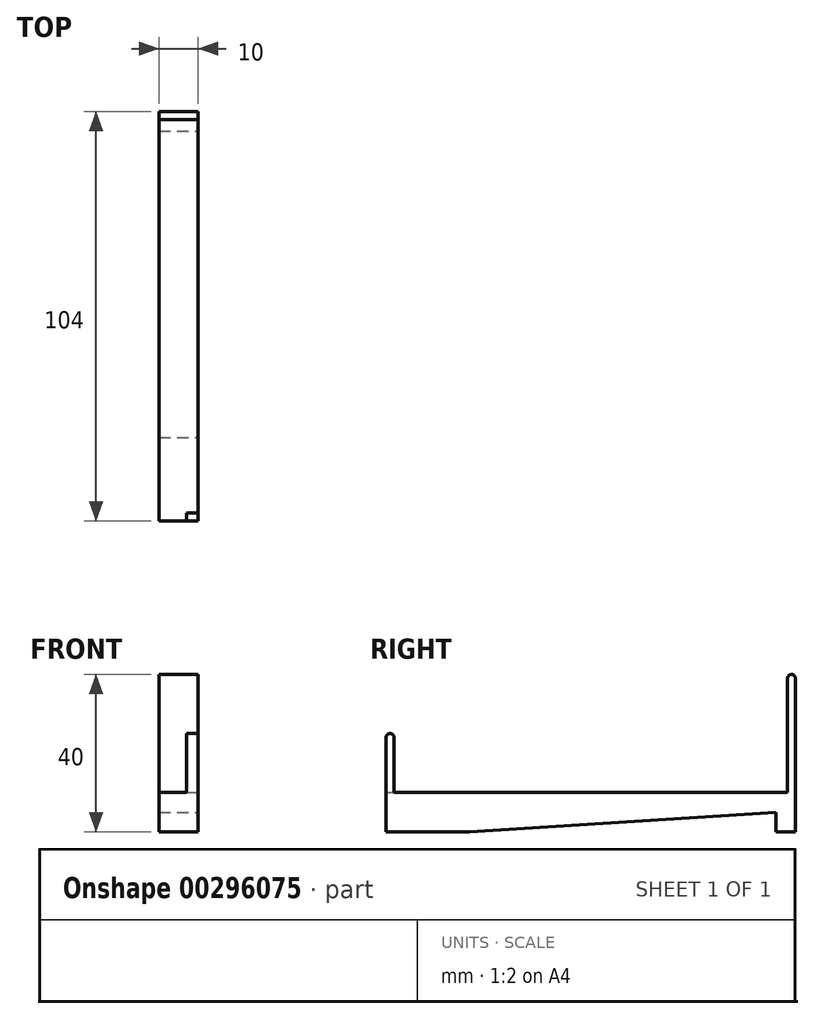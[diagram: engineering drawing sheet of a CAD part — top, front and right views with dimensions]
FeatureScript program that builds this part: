
annotation { "Feature Type Name" : "Feature", "Feature Type Description" : "" }
export const myFeature = defineFeature(function(context is Context, id is Id, definition is map)
    precondition{}
    {
        {
            var Q0;
            Q0=qCreatedBy(makeId("Top.planeOp"),FACE);
            var sketch = newSketch(context, id + "F0", { "sketchPlane" : qUnion([Q0])});
            skLineSegment(sketch, "E0.bottom", {"start": v(5, -52) * mm, "end": v(-5, -52) * mm});
            skLineSegment(sketch, "E0.top", {"start": v(5, 52) * mm, "end": v(-5, 52) * mm});
            skLineSegment(sketch, "E0.left", {"start": v(5, -52) * mm, "end": v(5, 52) * mm});
            skLineSegment(sketch, "E0.right", {"start": v(-5, -52) * mm, "end": v(-5, 52) * mm});
            skPoint(sketch, "E0.middle", {"position": v(0, 0) * mm});
            skSolve(sketch);
        }
        {
            var Q0;
            Q0=qSketchRegion(id+"F0",true);
            extrude(context, id + "F1", {"entities" : qUnion([Q0]), "depth" : 10 * mm});
        }
        {
            var Q0;
            Q0=makeQuery(id+"F1.opExtrude","CAP_FACE",FACE,{"disambiguationData":[OSD([sQuery(id+"F0.wireOp",EDGE,"E0.bottom"),sQuery(id+"F0.wireOp",EDGE,"E0.top"),sQuery(id+"F0.wireOp",EDGE,"E0.left"),sQuery(id+"F0.wireOp",EDGE,"E0.right")])],"isStart":false});
            var sketch = newSketch(context, id + "F2", { "sketchPlane" : qUnion([Q0])});
            skLineSegment(sketch, "E1.bottom", {"start": v(-5, -52) * mm, "end": v(5, -52) * mm});
            skLineSegment(sketch, "E1.top", {"start": v(-5, -50) * mm, "end": v(5, -50) * mm});
            skLineSegment(sketch, "E1.left", {"start": v(-5, -52) * mm, "end": v(-5, -50) * mm});
            skLineSegment(sketch, "E1.right", {"start": v(5, -52) * mm, "end": v(5, -50) * mm});
            skSolve(sketch);
        }
        {
            var Q0;
            Q0=qSketchRegion(id+"F2",true);
            extrude(context, id + "F3", {"entities" : qUnion([Q0]), "operationType" : NewBodyOperationType.ADD, "depth" : 15 * mm});
        }
        {
            var Q0;
            Q0=makeQuery(id+"F1.opExtrude","CAP_FACE",FACE,{"disambiguationData":[OSD([sQuery(id+"F0.wireOp",EDGE,"E0.bottom"),sQuery(id+"F0.wireOp",EDGE,"E0.top"),sQuery(id+"F0.wireOp",EDGE,"E0.left"),sQuery(id+"F0.wireOp",EDGE,"E0.right")])],"isStart":false});
            var sketch = newSketch(context, id + "F4", { "sketchPlane" : qUnion([Q0])});
            skLineSegment(sketch, "E2.bottom", {"start": v(-5, 52) * mm, "end": v(5, 52) * mm});
            skLineSegment(sketch, "E2.top", {"start": v(-5, 50) * mm, "end": v(5, 50) * mm});
            skLineSegment(sketch, "E2.left", {"start": v(-5, 52) * mm, "end": v(-5, 50) * mm});
            skLineSegment(sketch, "E2.right", {"start": v(5, 52) * mm, "end": v(5, 50) * mm});
            skSolve(sketch);
        }
        {
            var Q0;
            Q0=qSketchRegion(id+"F4",true);
            extrude(context, id + "F5", {"entities" : qUnion([Q0]), "operationType" : NewBodyOperationType.ADD, "depth" : 30 * mm});
        }
        {
            var Q0;
            Q0=makeQuery(id+"F5.boolean.opBoolean","MERGE",FACE,{"derivedFrom":[makeQuery(id+"F3.boolean.opBoolean","MERGE",FACE,{"derivedFrom":[makeQuery(id+"F1.opExtrude","SWEPT_FACE",FACE,{"disambiguationData":[OSD([sQuery(id+"F0.wireOp",EDGE,"E0.left")])]}),makeQuery(id+"F3.opExtrude","SWEPT_FACE",FACE,{"disambiguationData":[OSD([sQuery(id+"F2.wireOp",EDGE,"E1.right")])]})]}),makeQuery(id+"F5.opExtrude","SWEPT_FACE",FACE,{"disambiguationData":[OSD([sQuery(id+"F4.wireOp",EDGE,"E2.right")])]})]});
            var sketch = newSketch(context, id + "F6", { "sketchPlane" : qUnion([Q0])});
            skLineSegment(sketch, "E3", {"start": v(-30.84, 0) * mm, "end": v(47, 5) * mm});
            skLineSegment(sketch, "E4", {"start": v(47, 5) * mm, "end": v(47, 0) * mm});
            skLineSegment(sketch, "E5", {"start": v(47, 0) * mm, "end": v(-30.84, 0) * mm});
            skSolve(sketch);
        }
        {
            var Q0;
            Q0=qSketchRegion(id+"F6",true);
            extrude(context, id + "F7", {"entities" : qUnion([Q0]), "operationType" : NewBodyOperationType.REMOVE, "endBound" : BoundingType.THROUGH_ALL, "oppositeDirection" : true, "depth" : 25 * mm});
        }
        {
            var Q0;
            Q0=makeQuery(id+"F5.opExtrude","CAP_EDGE",EDGE,{"disambiguationData":[OSD([sQuery(id+"F4.wireOp",EDGE,"E2.top")])],"isStart":false});
            var Q1;
            Q1=makeQuery(id+"F5.opExtrude","CAP_EDGE",EDGE,{"disambiguationData":[OSD([sQuery(id+"F4.wireOp",EDGE,"E2.bottom")])],"isStart":false});
            var Q2;
            Q2=makeQuery(id+"F3.opExtrude","CAP_EDGE",EDGE,{"disambiguationData":[OSD([sQuery(id+"F2.wireOp",EDGE,"E1.bottom")])],"isStart":false});
            var Q3;
            Q3=makeQuery(id+"F3.opExtrude","CAP_EDGE",EDGE,{"disambiguationData":[OSD([sQuery(id+"F2.wireOp",EDGE,"E1.top")])],"isStart":false});
            var Q4;
            Q4=makeQuery(id+"F5.opExtrude","CAP_EDGE",EDGE,{"disambiguationData":[OSD([sQuery(id+"F4.wireOp",EDGE,"E2.top")])],"isStart":true});
            var Q5;
            Q5=makeQuery(id+"F3.opExtrude","CAP_EDGE",EDGE,{"disambiguationData":[OSD([sQuery(id+"F2.wireOp",EDGE,"E1.top")])],"isStart":true});
            fillet(context, id + "F8", {"entities" : qUnion([Q0, Q1, Q2, Q3, Q4, Q5]), "radius" : 1 * mm, "tangentPropagation" : true, "allowEdgeOverflow" : false});
        }
        {
            var Q0;
            Q0=makeQuery(id+"F5.boolean.opBoolean","MERGE",FACE,{"derivedFrom":[makeQuery(id+"F3.boolean.opBoolean","MERGE",FACE,{"derivedFrom":[makeQuery(id+"F1.opExtrude","SWEPT_FACE",FACE,{"disambiguationData":[OSD([sQuery(id+"F0.wireOp",EDGE,"E0.right")])]}),makeQuery(id+"F3.opExtrude","SWEPT_FACE",FACE,{"disambiguationData":[OSD([sQuery(id+"F2.wireOp",EDGE,"E1.left")])]})]}),makeQuery(id+"F5.opExtrude","SWEPT_FACE",FACE,{"disambiguationData":[OSD([sQuery(id+"F4.wireOp",EDGE,"E2.left")])]})]});
            var sketch = newSketch(context, id + "F9", { "sketchPlane" : qUnion([Q0])});
            skLineSegment(sketch, "E6.bottom", {"start": v(49, 10) * mm, "end": v(52, 10) * mm});
            skLineSegment(sketch, "E6.top", {"start": v(49, 25) * mm, "end": v(52, 25) * mm});
            skLineSegment(sketch, "E6.left", {"start": v(49, 10) * mm, "end": v(49, 25) * mm});
            skLineSegment(sketch, "E6.right", {"start": v(52, 10) * mm, "end": v(52, 25) * mm});
            skSolve(sketch);
        }
        {
            var Q0;
            Q0 = qSketchRegion(id + "F9", true);
            extrude(context, id + "F10", {"entities" : qUnion([Q0]), "operationType" : NewBodyOperationType.REMOVE, "oppositeDirection" : true, "depth" : 7 * mm});
        }
    });
